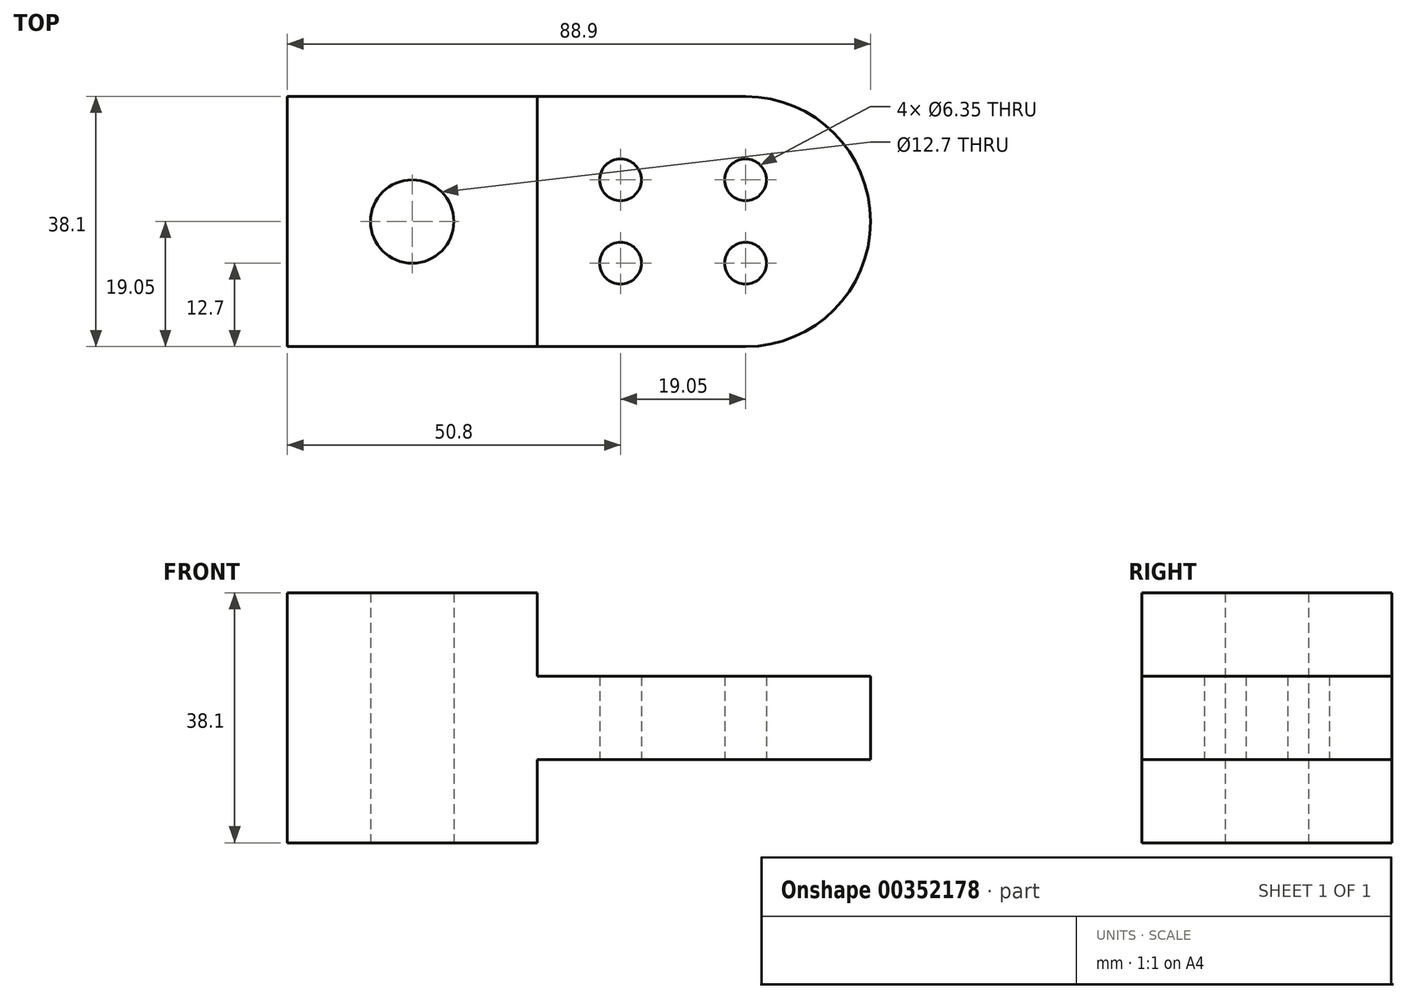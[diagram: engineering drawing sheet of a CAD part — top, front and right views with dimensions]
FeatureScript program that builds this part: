
annotation { "Feature Type Name" : "Feature", "Feature Type Description" : "" }
export const myFeature = defineFeature(function(context is Context, id is Id, definition is map)
    precondition{}
    {
        {
            var Q0;
            Q0=qCreatedBy(makeId("Top.planeOp"),FACE);
            var sketch = newSketch(context, id + "F0", { "sketchPlane" : qUnion([Q0])});
            skLineSegment(sketch, "E0.bottom", {"start": v(-38.1, 19.05) * mm, "end": v(0, 19.05) * mm});
            skLineSegment(sketch, "E0.top", {"start": v(-38.1, -19.05) * mm, "end": v(0, -19.05) * mm});
            skLineSegment(sketch, "E0.left", {"start": v(-38.1, 19.05) * mm, "end": v(-38.1, -19.05) * mm});
            skLineSegment(sketch, "E0.right", {"start": v(0, 19.05) * mm, "end": v(0, -19.05) * mm});
            skLineSegment(sketch, "E1", {"start": v(0, 19.05) * mm, "end": v(31.75, 19.05) * mm});
            skLineSegment(sketch, "E2", {"start": v(0, -19.05) * mm, "end": v(31.75, -19.05) * mm});
            skArc(sketch, "E3", {"start": v(31.75, 19.05) * mm, "mid": v(50.8, 0) * mm, "end": v(31.75, -19.05) * mm});
            skCircle(sketch, "E4", {"center": v(-19.05, 0) * mm, "radius": 6.35 * mm});
            skCircle(sketch, "E5", {"center": v(12.7, 6.35) * mm, "radius": 3.18 * mm});
            skCircle(sketch, "E6", {"center": v(31.75, 6.35) * mm, "radius": 3.18 * mm});
            skCircle(sketch, "E7", {"center": v(12.7, -6.35) * mm, "radius": 3.18 * mm});
            skCircle(sketch, "E8", {"center": v(31.75, -6.35) * mm, "radius": 3.18 * mm});
            skSolve(sketch);
        }
        {
            var Q0;
            Q0=makeQuery(id+"F0.imprint","IMPRINT",FACE,{"disambiguationData":[TD([[makeQuery(id+"F0.imprint","IMPRINT",EDGE,{"derivedFrom":sQuery(id+"F0.wireOp",EDGE,"E0.bottom")}),-1.0]])]});
            extrude(context, id + "F1", {"entities" : qUnion([Q0]), "depth" : 38.1 * mm, "symmetric" : true});
        }
        {
            var Q0;
            Q0=makeQuery(id+"F0.imprint","IMPRINT",FACE,{"disambiguationData":[TD([[makeQuery(id+"F0.imprint","IMPRINT",EDGE,{"derivedFrom":sQuery(id+"F0.wireOp",EDGE,"E0.right")}),1.0]])]});
            extrude(context, id + "F2", {"entities" : qUnion([Q0]), "operationType" : NewBodyOperationType.ADD, "depth" : 12.7 * mm, "symmetric" : true});
        }
    });
